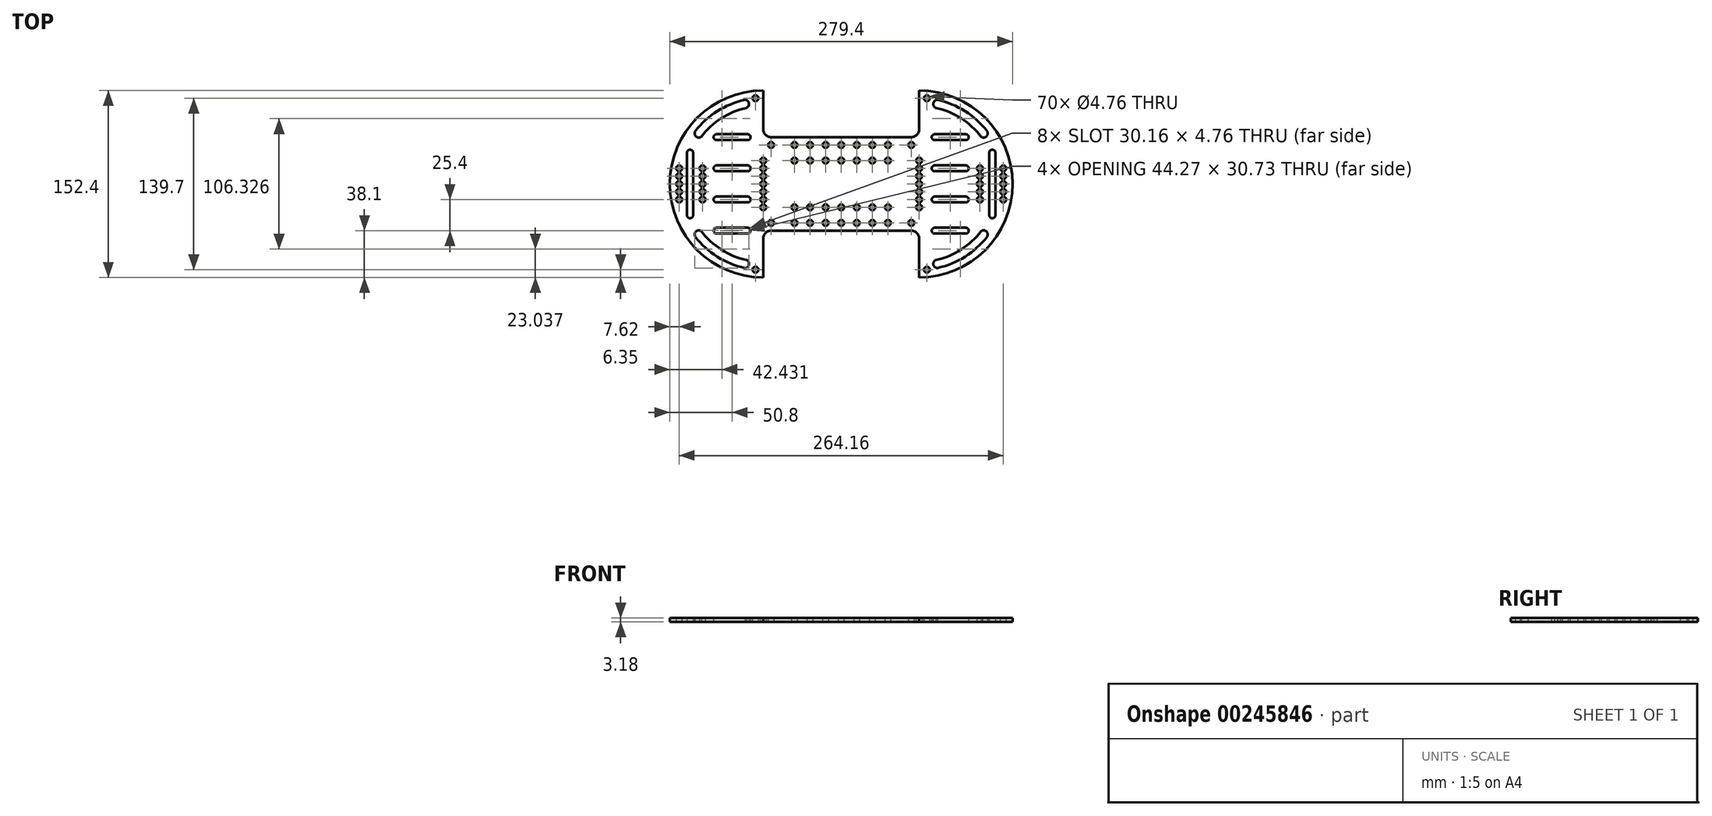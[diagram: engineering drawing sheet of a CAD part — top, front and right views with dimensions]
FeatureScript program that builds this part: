
annotation { "Feature Type Name" : "Feature", "Feature Type Description" : "" }
export const myFeature = defineFeature(function(context is Context, id is Id, definition is map)
    precondition{}
    {
        {
            var Q0;
            Q0=qCreatedBy(makeId("Top.planeOp"),FACE);
            var sketch = newSketch(context, id + "F0", { "sketchPlane" : qUnion([Q0])});
            skLineSegment(sketch, "E0.bottom", {"start": v(-57.15, 38.1) * mm, "end": v(57.15, 38.1) * mm});
            skLineSegment(sketch, "E0.top", {"start": v(-57.15, -38.1) * mm, "end": v(57.15, -38.1) * mm});
            skLineSegment(sketch, "E0.left", {"start": v(-63.5, 38.1) * mm, "end": v(-63.5, -38.1) * mm, "construction": true});
            skLineSegment(sketch, "E1.bottom", {"start": v(-123.2, 27.94) * mm, "end": v(-123.19, 27.94) * mm});
            skLineSegment(sketch, "E1.top", {"start": v(-123.19, -27.94) * mm, "end": v(-123.19, -27.94) * mm});
            skLineSegment(sketch, "E1.left", {"start": v(-125.73, 25.4) * mm, "end": v(-125.73, -25.4) * mm});
            skLineSegment(sketch, "E1.right", {"start": v(-120.65, 25.4) * mm, "end": v(-120.65, -25.4) * mm});
            skPoint(sketch, "E2.visualSharp", {"position": v(-125.73, 27.94) * mm});
            skArc(sketch, "E2.filletArc", {"start": v(-123.2, 27.94) * mm, "mid": v(-124.99, 27.2) * mm, "end": v(-125.73, 25.4) * mm});
            skPoint(sketch, "E3.visualSharp", {"position": v(-120.65, 27.94) * mm});
            skArc(sketch, "E3.filletArc", {"start": v(-120.65, 25.4) * mm, "mid": v(-121.4, 27.2) * mm, "end": v(-123.19, 27.94) * mm});
            skPoint(sketch, "E4.visualSharp", {"position": v(-120.65, -27.94) * mm});
            skArc(sketch, "E4.filletArc", {"start": v(-123.19, -27.94) * mm, "mid": v(-121.4, -27.2) * mm, "end": v(-120.65, -25.4) * mm});
            skPoint(sketch, "E5.visualSharp", {"position": v(-125.73, -27.94) * mm});
            skArc(sketch, "E5.filletArc", {"start": v(-125.73, -25.4) * mm, "mid": v(-124.99, -27.2) * mm, "end": v(-123.19, -27.94) * mm});
            skPoint(sketch, "E6", {"position": v(-120.65, 0) * mm});
            skLineSegment(sketch, "E7", {"start": v(-120.65, 0) * mm, "end": v(-63.5, 0) * mm, "construction": true});
            skLineSegment(sketch, "E8", {"start": v(-57.15, -24.13) * mm, "end": v(-57.15, 24.13) * mm, "construction": true});
            skPoint(sketch, "E9", {"position": v(-57.15, 0) * mm});
            skCircle(sketch, "E10", {"center": v(-57.15, 31.75) * mm, "radius": 2.38 * mm});
            skCircle(sketch, "E11.0.1.0", {"center": v(-57.15, -31.75) * mm, "radius": 2.38 * mm});
            skCircle(sketch, "E11.1.0.0", {"center": v(57.15, 31.75) * mm, "radius": 2.38 * mm});
            skCircle(sketch, "E11.1.1.0", {"center": v(57.15, -31.75) * mm, "radius": 2.38 * mm});
            skCircle(sketch, "E12", {"center": v(-132.08, 12.7) * mm, "radius": 2.38 * mm});
            skCircle(sketch, "E13", {"center": v(-132.08, 0) * mm, "radius": 2.38 * mm});
            skCircle(sketch, "E14", {"center": v(-132.08, 6.35) * mm, "radius": 2.38 * mm});
            skLineSegment(sketch, "E15", {"start": v(-132.08, 12.7) * mm, "end": v(-132.08, 6.35) * mm, "construction": true});
            skLineSegment(sketch, "E16", {"start": v(-132.08, 0) * mm, "end": v(-132.08, 6.35) * mm, "construction": true});
            skCircle(sketch, "E17", {"center": v(-132.08, -6.35) * mm, "radius": 2.38 * mm});
            skLineSegment(sketch, "E18", {"start": v(-132.08, 0) * mm, "end": v(-132.08, -6.35) * mm, "construction": true});
            skCircle(sketch, "E19", {"center": v(-132.08, -12.7) * mm, "radius": 2.38 * mm});
            skLineSegment(sketch, "E20", {"start": v(-132.08, -6.35) * mm, "end": v(-132.08, -12.7) * mm, "construction": true});
            skCircle(sketch, "E21.MirrorC", {"center": v(132.08, 12.7) * mm, "radius": 2.38 * mm});
            skArc(sketch, "E22.MirrorCS", {"start": v(123.2, 27.94) * mm, "mid": v(124.99, 27.2) * mm, "end": v(125.73, 25.4) * mm});
            skLineSegment(sketch, "E23.MirrorCS", {"start": v(120.65, 25.4) * mm, "end": v(120.65, -25.4) * mm});
            skArc(sketch, "E24.MirrorCS", {"start": v(123.19, -27.94) * mm, "mid": v(121.4, -27.2) * mm, "end": v(120.65, -25.4) * mm});
            skCircle(sketch, "E25.MirrorC", {"center": v(132.08, 6.35) * mm, "radius": 2.38 * mm});
            skCircle(sketch, "E26.MirrorC", {"center": v(132.08, -12.7) * mm, "radius": 2.38 * mm});
            skLineSegment(sketch, "E27.MirrorCS", {"start": v(125.73, 25.4) * mm, "end": v(125.73, -25.4) * mm});
            skArc(sketch, "E28.MirrorCS", {"start": v(120.65, 25.4) * mm, "mid": v(121.4, 27.2) * mm, "end": v(123.19, 27.94) * mm});
            skArc(sketch, "E29.MirrorCS", {"start": v(125.73, -25.4) * mm, "mid": v(124.99, -27.2) * mm, "end": v(123.19, -27.94) * mm});
            skCircle(sketch, "E30.MirrorC", {"center": v(132.08, 0) * mm, "radius": 2.38 * mm});
            skCircle(sketch, "E31.MirrorC", {"center": v(132.08, -6.35) * mm, "radius": 2.38 * mm});
            skCircle(sketch, "E32", {"center": v(-63.5, 19.05) * mm, "radius": 2.38 * mm});
            skCircle(sketch, "E33.0.1.0", {"center": v(-63.5, 12.7) * mm, "radius": 2.38 * mm});
            skCircle(sketch, "E33.0.2.0", {"center": v(-63.5, 6.35) * mm, "radius": 2.38 * mm});
            skCircle(sketch, "E33.0.3.0", {"center": v(-63.5, 0) * mm, "radius": 2.38 * mm});
            skCircle(sketch, "E33.0.4.0", {"center": v(-63.5, -6.35) * mm, "radius": 2.38 * mm});
            skCircle(sketch, "E33.0.5.0", {"center": v(-63.5, -12.7) * mm, "radius": 2.38 * mm});
            skCircle(sketch, "E33.0.6.0", {"center": v(-63.5, -19.05) * mm, "radius": 2.38 * mm});
            skLineSegment(sketch, "E33.direction1", {"start": v(-63.5, 19.05) * mm, "end": v(-38.1, 19.05) * mm, "construction": true});
            skLineSegment(sketch, "E33.direction2", {"start": v(-63.5, 19.05) * mm, "end": v(-63.5, 12.7) * mm, "construction": true});
            skCircle(sketch, "E34.MirrorC", {"center": v(63.5, 0) * mm, "radius": 2.38 * mm});
            skCircle(sketch, "E35.MirrorC", {"center": v(63.5, 19.05) * mm, "radius": 2.38 * mm});
            skCircle(sketch, "E36.MirrorC", {"center": v(63.5, -12.7) * mm, "radius": 2.38 * mm});
            skCircle(sketch, "E37.MirrorC", {"center": v(63.5, -6.35) * mm, "radius": 2.38 * mm});
            skCircle(sketch, "E38.MirrorC", {"center": v(63.5, -19.05) * mm, "radius": 2.38 * mm});
            skCircle(sketch, "E39.MirrorC", {"center": v(63.5, 12.7) * mm, "radius": 2.38 * mm});
            skCircle(sketch, "E40.MirrorC", {"center": v(63.5, 6.35) * mm, "radius": 2.38 * mm});
            skLineSegment(sketch, "E41", {"start": v(-63.5, 44.45) * mm, "end": v(-63.5, 76.2) * mm});
            skLineSegment(sketch, "E42", {"start": v(-63.5, -44.45) * mm, "end": v(-63.5, -76.2) * mm});
            skArc(sketch, "E43", {"start": v(-63.5, 76.2) * mm, "mid": v(-139.7, 0) * mm, "end": v(-63.5, -76.2) * mm});
            skLineSegment(sketch, "E44", {"start": v(-63.5, -76.2) * mm, "end": v(-50.05, -76.2) * mm, "construction": true});
            skLineSegment(sketch, "E45.MirrorCS", {"start": v(63.5, -44.45) * mm, "end": v(63.5, -76.2) * mm});
            skArc(sketch, "E46.MirrorCS", {"start": v(63.5, 76.2) * mm, "mid": v(139.7, 0) * mm, "end": v(63.5, -76.2) * mm});
            skLineSegment(sketch, "E47.MirrorCS", {"start": v(63.5, 44.45) * mm, "end": v(63.5, 76.2) * mm});
            skPoint(sketch, "E48.visualSharp", {"position": v(-63.5, -38.1) * mm});
            skArc(sketch, "E48.filletArc", {"start": v(-57.15, -38.1) * mm, "mid": v(-61.64, -39.96) * mm, "end": v(-63.5, -44.45) * mm});
            skPoint(sketch, "E49.visualSharp", {"position": v(63.5, -38.1) * mm});
            skArc(sketch, "E49.filletArc", {"start": v(63.5, -44.45) * mm, "mid": v(61.64, -39.96) * mm, "end": v(57.15, -38.1) * mm});
            skPoint(sketch, "E50.visualSharp", {"position": v(-63.5, 38.1) * mm});
            skArc(sketch, "E50.filletArc", {"start": v(-63.5, 44.45) * mm, "mid": v(-61.64, 39.96) * mm, "end": v(-57.15, 38.1) * mm});
            skPoint(sketch, "E51.visualSharp", {"position": v(63.5, 38.1) * mm});
            skArc(sketch, "E51.filletArc", {"start": v(57.15, 38.1) * mm, "mid": v(61.64, 39.96) * mm, "end": v(63.5, 44.45) * mm});
            skCircle(sketch, "E52", {"center": v(-69.85, 69.85) * mm, "radius": 2.38 * mm});
            skLineSegment(sketch, "E53", {"start": v(-63.5, 76.2) * mm, "end": v(-79.1, 76.2) * mm, "construction": true});
            skCircle(sketch, "E54.0.1.0", {"center": v(-69.85, -69.85) * mm, "radius": 2.38 * mm});
            skCircle(sketch, "E54.1.0.0", {"center": v(69.85, 69.85) * mm, "radius": 2.38 * mm});
            skCircle(sketch, "E54.1.1.0", {"center": v(69.85, -69.85) * mm, "radius": 2.38 * mm});
            skLineSegment(sketch, "E54.direction1", {"start": v(-69.85, 69.85) * mm, "end": v(69.85, 69.85) * mm, "construction": true});
            skLineSegment(sketch, "E54.direction2", {"start": v(-69.85, 69.85) * mm, "end": v(-69.85, -69.85) * mm, "construction": true});
            skCircle(sketch, "E55.1.0.0", {"center": v(-113.03, -12.7) * mm, "radius": 2.38 * mm});
            skCircle(sketch, "E55.1.0.1", {"center": v(-113.03, 12.7) * mm, "radius": 2.38 * mm});
            skCircle(sketch, "E55.1.0.2", {"center": v(-113.03, 6.35) * mm, "radius": 2.38 * mm});
            skCircle(sketch, "E55.1.0.3", {"center": v(-113.03, 0) * mm, "radius": 2.38 * mm});
            skCircle(sketch, "E55.1.0.4", {"center": v(-113.03, -6.35) * mm, "radius": 2.38 * mm});
            skLineSegment(sketch, "E55.direction1", {"start": v(-132.08, -12.7) * mm, "end": v(-113.03, -12.7) * mm, "construction": true});
            skArc(sketch, "E56", {"start": v(-78.44, -68.53) * mm, "mid": v(-100.96, -59.3) * mm, "end": v(-118.96, -42.94) * mm});
            skArc(sketch, "E57", {"start": v(-114.03, -38.45) * mm, "mid": v(-97.73, -53.48) * mm, "end": v(-77.26, -62) * mm});
            skArc(sketch, "E58", {"start": v(76.2, 40.48) * mm, "mid": v(73.82, 38.1) * mm, "end": v(76.2, 35.72) * mm});
            skLineSegment(sketch, "E59", {"start": v(76.2, 40.48) * mm, "end": v(101.6, 40.48) * mm});
            skLineSegment(sketch, "E60", {"start": v(76.2, 35.72) * mm, "end": v(101.6, 35.72) * mm});
            skArc(sketch, "E61", {"start": v(101.6, 40.48) * mm, "mid": v(103.98, 38.1) * mm, "end": v(101.6, 35.72) * mm});
            skArc(sketch, "E62", {"start": v(-114.03, -38.45) * mm, "mid": v(-118.33, -38.68) * mm, "end": v(-118.96, -42.94) * mm});
            skPoint(sketch, "E63.orphan", {"position": v(-122.16, -38.45) * mm});
            skArc(sketch, "E64", {"start": v(-78.44, -68.53) * mm, "mid": v(-75.14, -65.75) * mm, "end": v(-77.26, -62) * mm});
            skArc(sketch, "E65.MirrorCS", {"start": v(-78.44, 68.53) * mm, "mid": v(-75.14, 65.75) * mm, "end": v(-77.26, 62) * mm});
            skArc(sketch, "E66.MirrorCS", {"start": v(-114.03, 38.45) * mm, "mid": v(-97.73, 53.48) * mm, "end": v(-77.26, 62) * mm});
            skArc(sketch, "E67.MirrorCS", {"start": v(-114.03, 38.45) * mm, "mid": v(-118.33, 38.68) * mm, "end": v(-118.96, 42.94) * mm});
            skArc(sketch, "E68.MirrorCS", {"start": v(-78.44, 68.53) * mm, "mid": v(-100.96, 59.3) * mm, "end": v(-118.96, 42.94) * mm});
            skArc(sketch, "E69.MirrorCS", {"start": v(114.03, 38.45) * mm, "mid": v(97.73, 53.48) * mm, "end": v(77.26, 62) * mm});
            skArc(sketch, "E70.MirrorCS", {"start": v(78.44, -68.53) * mm, "mid": v(100.96, -59.3) * mm, "end": v(118.96, -42.94) * mm});
            skArc(sketch, "E71.MirrorCS", {"start": v(114.03, 38.45) * mm, "mid": v(118.33, 38.68) * mm, "end": v(118.96, 42.94) * mm});
            skArc(sketch, "E72.MirrorCS", {"start": v(114.03, -38.45) * mm, "mid": v(118.33, -38.68) * mm, "end": v(118.96, -42.94) * mm});
            skArc(sketch, "E73.MirrorCS", {"start": v(78.44, -68.53) * mm, "mid": v(75.14, -65.75) * mm, "end": v(77.26, -62) * mm});
            skArc(sketch, "E74.MirrorCS", {"start": v(78.44, 68.53) * mm, "mid": v(100.96, 59.3) * mm, "end": v(118.96, 42.94) * mm});
            skArc(sketch, "E75.MirrorCS", {"start": v(114.03, -38.45) * mm, "mid": v(97.73, -53.48) * mm, "end": v(77.26, -62) * mm});
            skArc(sketch, "E76.MirrorCS", {"start": v(78.44, 68.53) * mm, "mid": v(75.14, 65.75) * mm, "end": v(77.26, 62) * mm});
            skArc(sketch, "E77.0.1.0", {"start": v(76.2, 15.08) * mm, "mid": v(73.82, 12.7) * mm, "end": v(76.2, 10.32) * mm});
            skLineSegment(sketch, "E77.0.1.1", {"start": v(76.2, 10.32) * mm, "end": v(101.6, 10.32) * mm});
            skArc(sketch, "E77.0.1.2", {"start": v(101.6, 15.08) * mm, "mid": v(103.98, 12.7) * mm, "end": v(101.6, 10.32) * mm});
            skLineSegment(sketch, "E77.0.1.3", {"start": v(76.2, 15.08) * mm, "end": v(101.6, 15.08) * mm});
            skArc(sketch, "E77.0.2.0", {"start": v(76.2, -10.32) * mm, "mid": v(73.82, -12.7) * mm, "end": v(76.2, -15.08) * mm});
            skLineSegment(sketch, "E77.0.2.1", {"start": v(76.2, -15.08) * mm, "end": v(101.6, -15.08) * mm});
            skArc(sketch, "E77.0.2.2", {"start": v(101.6, -10.32) * mm, "mid": v(103.98, -12.7) * mm, "end": v(101.6, -15.08) * mm});
            skLineSegment(sketch, "E77.0.2.3", {"start": v(76.2, -10.32) * mm, "end": v(101.6, -10.32) * mm});
            skArc(sketch, "E77.0.3.0", {"start": v(76.2, -35.72) * mm, "mid": v(73.82, -38.1) * mm, "end": v(76.2, -40.48) * mm});
            skLineSegment(sketch, "E77.0.3.1", {"start": v(76.2, -40.48) * mm, "end": v(101.6, -40.48) * mm});
            skArc(sketch, "E77.0.3.2", {"start": v(101.6, -35.72) * mm, "mid": v(103.98, -38.1) * mm, "end": v(101.6, -40.48) * mm});
            skLineSegment(sketch, "E77.0.3.3", {"start": v(76.2, -35.72) * mm, "end": v(101.6, -35.72) * mm});
            skLineSegment(sketch, "E77.direction1", {"start": v(76.2, 35.72) * mm, "end": v(101.6, 35.72) * mm, "construction": true});
            skLineSegment(sketch, "E78.MirrorCS", {"start": v(-76.2, -15.08) * mm, "end": v(-101.6, -15.08) * mm});
            skArc(sketch, "E79.MirrorCS", {"start": v(-101.6, 15.08) * mm, "mid": v(-103.98, 12.7) * mm, "end": v(-101.6, 10.32) * mm});
            skLineSegment(sketch, "E80.MirrorCS", {"start": v(-76.2, -35.72) * mm, "end": v(-101.6, -35.72) * mm});
            skLineSegment(sketch, "E81.MirrorCS", {"start": v(-76.2, 40.48) * mm, "end": v(-101.6, 40.48) * mm});
            skLineSegment(sketch, "E82.MirrorCS", {"start": v(-76.2, -10.32) * mm, "end": v(-101.6, -10.32) * mm});
            skArc(sketch, "E83.MirrorCS", {"start": v(-101.6, 40.48) * mm, "mid": v(-103.98, 38.1) * mm, "end": v(-101.6, 35.72) * mm});
            skArc(sketch, "E84.MirrorCS", {"start": v(-76.2, -10.32) * mm, "mid": v(-73.82, -12.7) * mm, "end": v(-76.2, -15.08) * mm});
            skLineSegment(sketch, "E85.MirrorCS", {"start": v(-76.2, -40.48) * mm, "end": v(-101.6, -40.48) * mm});
            skLineSegment(sketch, "E86.MirrorCS", {"start": v(-76.2, 10.32) * mm, "end": v(-101.6, 10.32) * mm});
            skArc(sketch, "E87.MirrorCS", {"start": v(-101.6, -35.72) * mm, "mid": v(-103.98, -38.1) * mm, "end": v(-101.6, -40.48) * mm});
            skArc(sketch, "E88.MirrorCS", {"start": v(-76.2, 40.48) * mm, "mid": v(-73.82, 38.1) * mm, "end": v(-76.2, 35.72) * mm});
            skArc(sketch, "E89.MirrorCS", {"start": v(-101.6, -10.32) * mm, "mid": v(-103.98, -12.7) * mm, "end": v(-101.6, -15.08) * mm});
            skLineSegment(sketch, "E90.MirrorCS", {"start": v(-76.2, 35.72) * mm, "end": v(-101.6, 35.72) * mm, "construction": true});
            skLineSegment(sketch, "E91.MirrorCS", {"start": v(-76.2, 35.72) * mm, "end": v(-101.6, 35.72) * mm});
            skLineSegment(sketch, "E92.MirrorCS", {"start": v(-76.2, 15.08) * mm, "end": v(-101.6, 15.08) * mm});
            skArc(sketch, "E93.MirrorCS", {"start": v(-76.2, -35.72) * mm, "mid": v(-73.82, -38.1) * mm, "end": v(-76.2, -40.48) * mm});
            skArc(sketch, "E94.MirrorCS", {"start": v(-76.2, 15.08) * mm, "mid": v(-73.82, 12.7) * mm, "end": v(-76.2, 10.32) * mm});
            skCircle(sketch, "E95", {"center": v(-38.1, -31.75) * mm, "radius": 2.38 * mm});
            skCircle(sketch, "E96.0.1.0", {"center": v(-38.1, -19.05) * mm, "radius": 2.38 * mm});
            skCircle(sketch, "E96.1.0.0", {"center": v(-25.4, -31.75) * mm, "radius": 2.38 * mm});
            skCircle(sketch, "E96.1.1.0", {"center": v(-25.4, -19.05) * mm, "radius": 2.38 * mm});
            skCircle(sketch, "E96.2.0.0", {"center": v(-12.7, -31.75) * mm, "radius": 2.38 * mm});
            skCircle(sketch, "E96.2.1.0", {"center": v(-12.7, -19.05) * mm, "radius": 2.38 * mm});
            skCircle(sketch, "E96.3.0.0", {"center": v(0, -31.75) * mm, "radius": 2.38 * mm});
            skCircle(sketch, "E96.3.1.0", {"center": v(0, -19.05) * mm, "radius": 2.38 * mm});
            skCircle(sketch, "E96.4.0.0", {"center": v(12.7, -31.75) * mm, "radius": 2.38 * mm});
            skCircle(sketch, "E96.4.1.0", {"center": v(12.7, -19.05) * mm, "radius": 2.38 * mm});
            skCircle(sketch, "E96.5.0.0", {"center": v(25.4, -31.75) * mm, "radius": 2.38 * mm});
            skCircle(sketch, "E96.5.1.0", {"center": v(25.4, -19.05) * mm, "radius": 2.38 * mm});
            skCircle(sketch, "E96.6.0.0", {"center": v(38.1, -31.75) * mm, "radius": 2.38 * mm});
            skCircle(sketch, "E96.6.1.0", {"center": v(38.1, -19.05) * mm, "radius": 2.38 * mm});
            skLineSegment(sketch, "E96.direction1", {"start": v(-38.1, -31.75) * mm, "end": v(-25.4, -31.75) * mm, "construction": true});
            skCircle(sketch, "E97.MirrorC", {"center": v(-12.7, 19.05) * mm, "radius": 2.38 * mm});
            skCircle(sketch, "E98.MirrorC", {"center": v(38.1, 31.75) * mm, "radius": 2.38 * mm});
            skCircle(sketch, "E99.MirrorC", {"center": v(0, 31.75) * mm, "radius": 2.38 * mm});
            skCircle(sketch, "E100.MirrorC", {"center": v(-25.4, 31.75) * mm, "radius": 2.38 * mm});
            skCircle(sketch, "E101.MirrorC", {"center": v(38.1, 19.05) * mm, "radius": 2.38 * mm});
            skCircle(sketch, "E102.MirrorC", {"center": v(12.7, 19.05) * mm, "radius": 2.38 * mm});
            skCircle(sketch, "E103.MirrorC", {"center": v(0, 19.05) * mm, "radius": 2.38 * mm});
            skCircle(sketch, "E104.MirrorC", {"center": v(-25.4, 19.05) * mm, "radius": 2.38 * mm});
            skCircle(sketch, "E105.MirrorC", {"center": v(25.4, 31.75) * mm, "radius": 2.38 * mm});
            skCircle(sketch, "E106.MirrorC", {"center": v(-38.1, 31.75) * mm, "radius": 2.38 * mm});
            skLineSegment(sketch, "E107.MirrorCS", {"start": v(-38.1, 31.75) * mm, "end": v(-25.4, 31.75) * mm, "construction": true});
            skCircle(sketch, "E108.MirrorC", {"center": v(-12.7, 31.75) * mm, "radius": 2.38 * mm});
            skCircle(sketch, "E109.MirrorC", {"center": v(-38.1, 19.05) * mm, "radius": 2.38 * mm});
            skCircle(sketch, "E110.MirrorC", {"center": v(25.4, 19.05) * mm, "radius": 2.38 * mm});
            skCircle(sketch, "E111.MirrorC", {"center": v(12.7, 31.75) * mm, "radius": 2.38 * mm});
            skCircle(sketch, "E112.MirrorC", {"center": v(113.03, -12.7) * mm, "radius": 2.38 * mm});
            skCircle(sketch, "E113.MirrorC", {"center": v(113.03, -6.35) * mm, "radius": 2.38 * mm});
            skCircle(sketch, "E114.MirrorC", {"center": v(113.03, 0) * mm, "radius": 2.38 * mm});
            skCircle(sketch, "E115.MirrorC", {"center": v(113.03, 6.35) * mm, "radius": 2.38 * mm});
            skCircle(sketch, "E116.MirrorC", {"center": v(113.03, 12.7) * mm, "radius": 2.38 * mm});
            skSolve(sketch);
        }
        {
            var Q0;
            Q0=makeQuery(id+"F0.imprint","IMPRINT",FACE,{"disambiguationData":[TD([[makeQuery(id+"F0.imprint","IMPRINT",EDGE,{"derivedFrom":sQuery(id+"F0.wireOp",EDGE,"E0.bottom")}),-1.0]])]});
            extrude(context, id + "F1", {"entities" : qUnion([Q0]), "depth" : 3.17 * mm});
        }
    });
